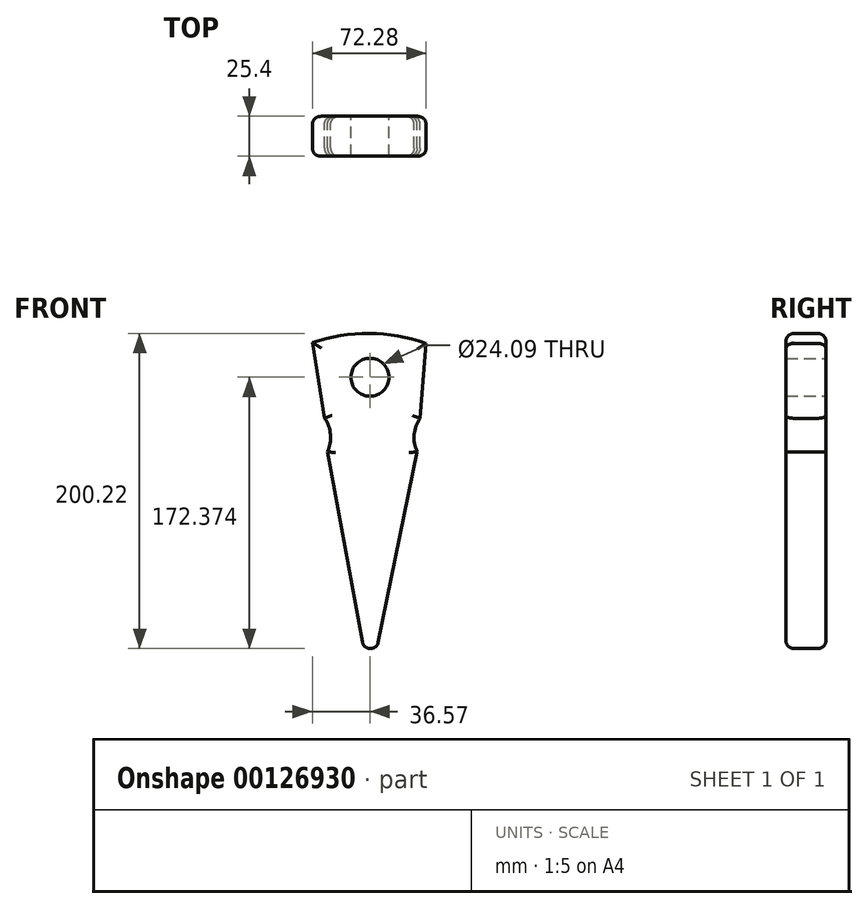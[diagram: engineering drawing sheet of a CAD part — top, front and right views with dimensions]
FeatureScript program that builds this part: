
annotation { "Feature Type Name" : "Feature", "Feature Type Description" : "" }
export const myFeature = defineFeature(function(context is Context, id is Id, definition is map)
    precondition{}
    {
        {
            var Q0;
            Q0=qCreatedBy(makeId("Front.planeOp"),FACE);
            var sketch = newSketch(context, id + "F0", { "sketchPlane" : qUnion([Q0])});
            skArc(sketch, "E0", {"start": v(35.7, 35.8) * mm, "mid": v(-0.38, 42.16) * mm, "end": v(-36.57, 36.39) * mm});
            skLineSegment(sketch, "E1", {"start": v(-36.57, 36.39) * mm, "end": v(-28.82, -11.75) * mm});
            skLineSegment(sketch, "E2", {"start": v(35.7, 35.8) * mm, "end": v(31.86, -11.75) * mm});
            skArc(sketch, "E3", {"start": v(-26.99, -33.03) * mm, "mid": v(-25.03, -22.14) * mm, "end": v(-28.82, -11.75) * mm});
            skArc(sketch, "E4", {"start": v(31.86, -11.75) * mm, "mid": v(28.08, -22.14) * mm, "end": v(30.04, -33.03) * mm});
            skLineSegment(sketch, "E5", {"start": v(-26.99, -33.03) * mm, "end": v(0, -179.58) * mm});
            skLineSegment(sketch, "E6", {"start": v(0, -179.58) * mm, "end": v(30.04, -33.03) * mm});
            skCircle(sketch, "E7", {"center": v(0, 14.31) * mm, "radius": 12.04 * mm});
            skSolve(sketch);
        }
        {
            var Q0;
            Q0=makeQuery(id+"F0.imprint","IMPRINT",FACE,{"disambiguationData":[TD([[makeQuery(id+"F0.imprint","IMPRINT",EDGE,{"derivedFrom":sQuery(id+"F0.wireOp",EDGE,"E0")}),1.0]])]});
            extrude(context, id + "F1", {"entities" : qUnion([Q0]), "depth" : 25.4 * mm});
        }
        {
            var Q0;
            Q0=makeQuery(id+"F1.opExtrude","CAP_EDGE",EDGE,{"disambiguationData":[OSD([sQuery(id+"F0.wireOp",EDGE,"E1")])],"isStart":false});
            var Q1;
            Q1=makeQuery(id+"F1.opExtrude","CAP_EDGE",EDGE,{"disambiguationData":[OSD([sQuery(id+"F0.wireOp",EDGE,"E1")])],"isStart":true});
            var Q2;
            Q2=makeQuery(id+"F1.opExtrude","CAP_EDGE",EDGE,{"disambiguationData":[OSD([sQuery(id+"F0.wireOp",EDGE,"E3")])],"isStart":false});
            var Q3;
            Q3=makeQuery(id+"F1.opExtrude","CAP_EDGE",EDGE,{"disambiguationData":[OSD([sQuery(id+"F0.wireOp",EDGE,"E3")])],"isStart":true});
            var Q4;
            Q4=makeQuery(id+"F1.opExtrude","CAP_EDGE",EDGE,{"disambiguationData":[OSD([sQuery(id+"F0.wireOp",EDGE,"E5")])],"isStart":false});
            var Q5;
            Q5=makeQuery(id+"F1.opExtrude","CAP_EDGE",EDGE,{"disambiguationData":[OSD([sQuery(id+"F0.wireOp",EDGE,"E5")])],"isStart":true});
            var Q6;
            Q6=makeQuery(id+"F1.opExtrude","CAP_EDGE",EDGE,{"disambiguationData":[OSD([sQuery(id+"F0.wireOp",EDGE,"E0")])],"isStart":false});
            var Q7;
            Q7=makeQuery(id+"F1.opExtrude","CAP_EDGE",EDGE,{"disambiguationData":[OSD([sQuery(id+"F0.wireOp",EDGE,"E0")])],"isStart":true});
            var Q8;
            Q8=makeQuery(id+"F1.opExtrude","CAP_EDGE",EDGE,{"disambiguationData":[OSD([sQuery(id+"F0.wireOp",EDGE,"E2")])],"isStart":false});
            var Q9;
            Q9=makeQuery(id+"F1.opExtrude","CAP_EDGE",EDGE,{"disambiguationData":[OSD([sQuery(id+"F0.wireOp",EDGE,"E2")])],"isStart":true});
            var Q10;
            Q10=makeQuery(id+"F1.opExtrude","CAP_EDGE",EDGE,{"disambiguationData":[OSD([sQuery(id+"F0.wireOp",EDGE,"E4")])],"isStart":false});
            var Q11;
            Q11=makeQuery(id+"F1.opExtrude","CAP_EDGE",EDGE,{"disambiguationData":[OSD([sQuery(id+"F0.wireOp",EDGE,"E4")])],"isStart":true});
            var Q12;
            Q12=makeQuery(id+"F1.opExtrude","CAP_EDGE",EDGE,{"disambiguationData":[OSD([sQuery(id+"F0.wireOp",EDGE,"E6")])],"isStart":true});
            var Q13;
            Q13=makeQuery(id+"F1.opExtrude","CAP_EDGE",EDGE,{"disambiguationData":[OSD([sQuery(id+"F0.wireOp",EDGE,"E6")])],"isStart":false});
            fillet(context, id + "F2", {"entities" : qUnion([Q0, Q1, Q2, Q3, Q4, Q5, Q6, Q7, Q8, Q9, Q10, Q11, Q12, Q13]), "radius" : 5.08 * mm, "tangentPropagation" : true, "allowEdgeOverflow" : false});
        }
        {
            var Q0;
            Q0=makeQuery(id+"F1.opExtrude","SWEPT_EDGE",EDGE,{"disambiguationData":[OSD([sQuery(id+"F0.wireOp",EDGE,"E5"),sQuery(id+"F0.wireOp",EDGE,"E6")])]});
            fillet(context, id + "F3", {"entities" : qUnion([Q0]), "radius" : 5.08 * mm, "tangentPropagation" : true, "allowEdgeOverflow" : false});
        }
    });
